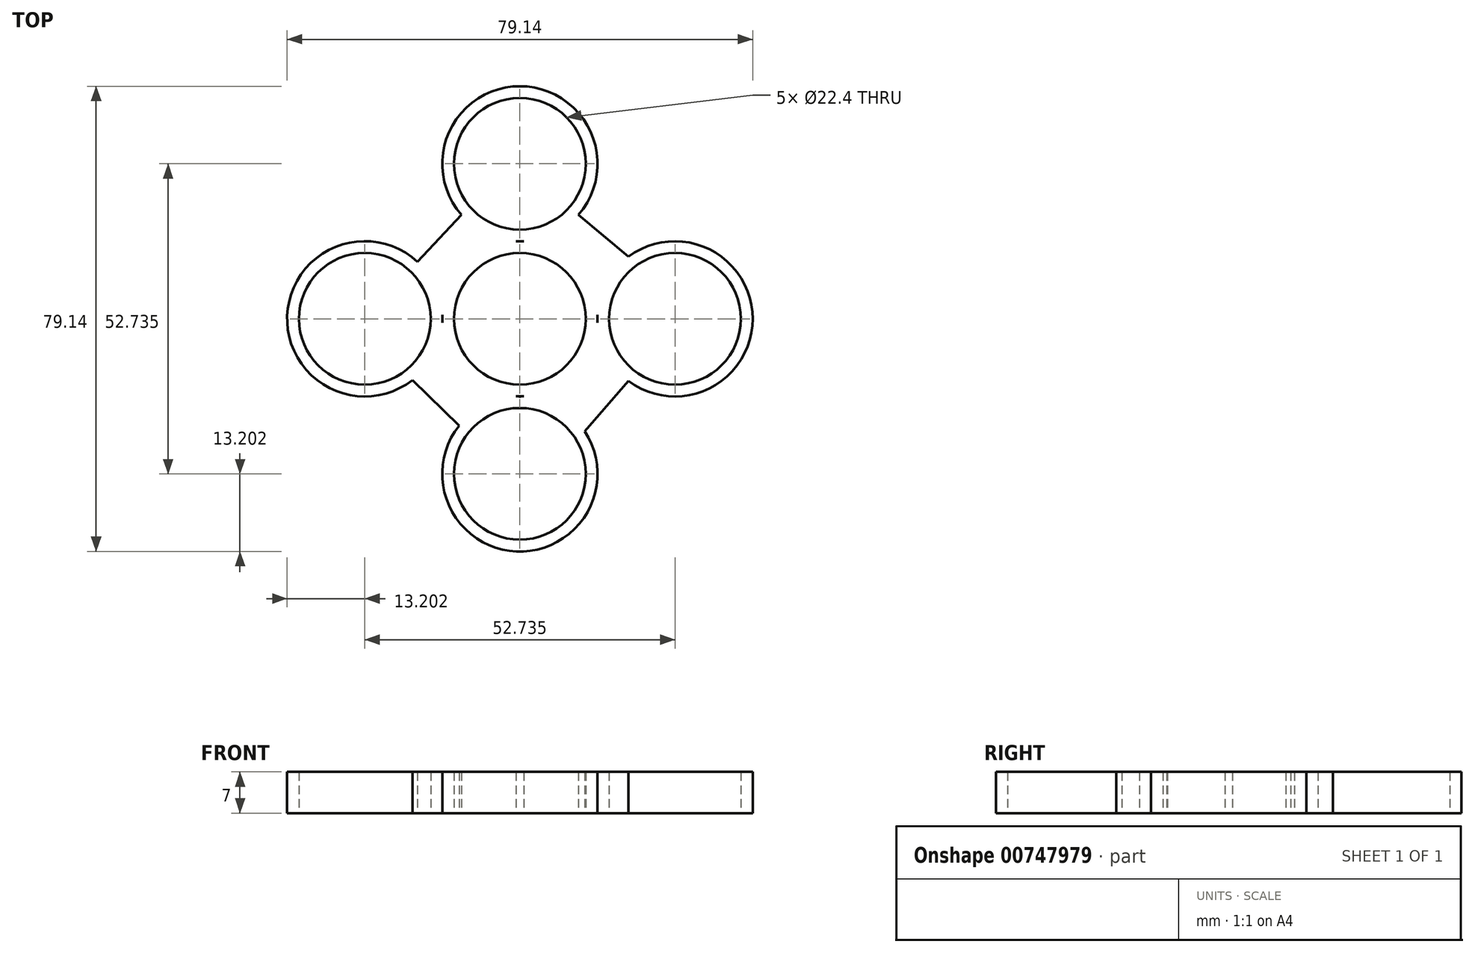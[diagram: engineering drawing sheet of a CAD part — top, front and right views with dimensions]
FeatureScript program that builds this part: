
annotation { "Feature Type Name" : "Feature", "Feature Type Description" : "" }
export const myFeature = defineFeature(function(context is Context, id is Id, definition is map)
    precondition{}
    {
        {
            var Q0;
            Q0=qCreatedBy(makeId("Top.planeOp"),FACE);
            var sketch = newSketch(context, id + "F0", { "sketchPlane" : qUnion([Q0])});
            skCircle(sketch, "E0", {"center": v(0, 0) * mm, "radius": 11.2 * mm});
            skArc(sketch, "E1", {"start": v(-0.65, -13.18) * mm, "mid": v(0, -13.2) * mm, "end": v(0.65, -13.18) * mm});
            skCircle(sketch, "E2", {"center": v(0, 26.37) * mm, "radius": 11.2 * mm});
            skArc(sketch, "E3", {"start": v(9.96, 17.7) * mm, "mid": v(0, 39.57) * mm, "end": v(-9.96, 17.7) * mm});
            skCircle(sketch, "E4.1.0", {"center": v(-26.37, 0) * mm, "radius": 11.2 * mm});
            skArc(sketch, "E4.1.1", {"start": v(-17.4, 9.7) * mm, "mid": v(-39.56, 0.56) * mm, "end": v(-18.27, -10.42) * mm});
            skCircle(sketch, "E4.2.0", {"center": v(0, -26.37) * mm, "radius": 11.2 * mm});
            skArc(sketch, "E4.2.1", {"start": v(-10.34, -18.16) * mm, "mid": v(-0.6, -39.55) * mm, "end": v(11.03, -19.12) * mm});
            skCircle(sketch, "E4.3.0", {"center": v(26.37, 0) * mm, "radius": 11.2 * mm});
            skArc(sketch, "E4.3.1", {"start": v(13.18, 0.65) * mm, "mid": v(13.17, 0) * mm, "end": v(13.18, -0.65) * mm});
            skLineSegment(sketch, "E5", {"start": v(-17.4, 9.7) * mm, "end": v(-9.96, 17.7) * mm});
            skLineSegment(sketch, "E6", {"start": v(9.96, 17.7) * mm, "end": v(18.45, 10.56) * mm});
            skLineSegment(sketch, "E7", {"start": v(-9.96, -18.53) * mm, "end": v(-18.27, -10.42) * mm});
            skArc(sketch, "E8.trimOffspring", {"start": v(18.45, -10.56) * mm, "mid": v(39.57, 0) * mm, "end": v(18.45, 10.56) * mm});
            skArc(sketch, "E9.trimOffspring", {"start": v(-13.18, 0.65) * mm, "mid": v(-13.2, 0) * mm, "end": v(-13.18, -0.65) * mm});
            skArc(sketch, "E10.trimOffspring", {"start": v(0.65, 13.18) * mm, "mid": v(0, 13.2) * mm, "end": v(-0.65, 13.18) * mm});
            skArc(sketch, "E11.trimOffspring", {"start": v(13.18, -0.65) * mm, "mid": v(13.2, 0) * mm, "end": v(13.18, 0.65) * mm});
            skArc(sketch, "E12.trimOffspring", {"start": v(-13.18, -0.65) * mm, "mid": v(-13.17, 0) * mm, "end": v(-13.18, 0.65) * mm});
            skArc(sketch, "E13.trimOffspring", {"start": v(-0.65, 13.18) * mm, "mid": v(0, 13.17) * mm, "end": v(0.65, 13.18) * mm});
            skPoint(sketch, "E14.end.orphan", {"position": v(11.03, -18.53) * mm});
            skLineSegment(sketch, "E15", {"start": v(18.45, -10.56) * mm, "end": v(11.03, -19.12) * mm});
            skArc(sketch, "E16.trimOffspring", {"start": v(0.65, -13.18) * mm, "mid": v(0, -13.17) * mm, "end": v(-0.65, -13.18) * mm});
            skSolve(sketch);
        }
        {
            var Q0;
            Q0 = qSketchRegion(id + "F0", true);
            extrude(context, id + "F1", {"entities" : qUnion([Q0]), "depth" : 7 * mm, "offsetDistance" : 25 * mm});
        }
    });
